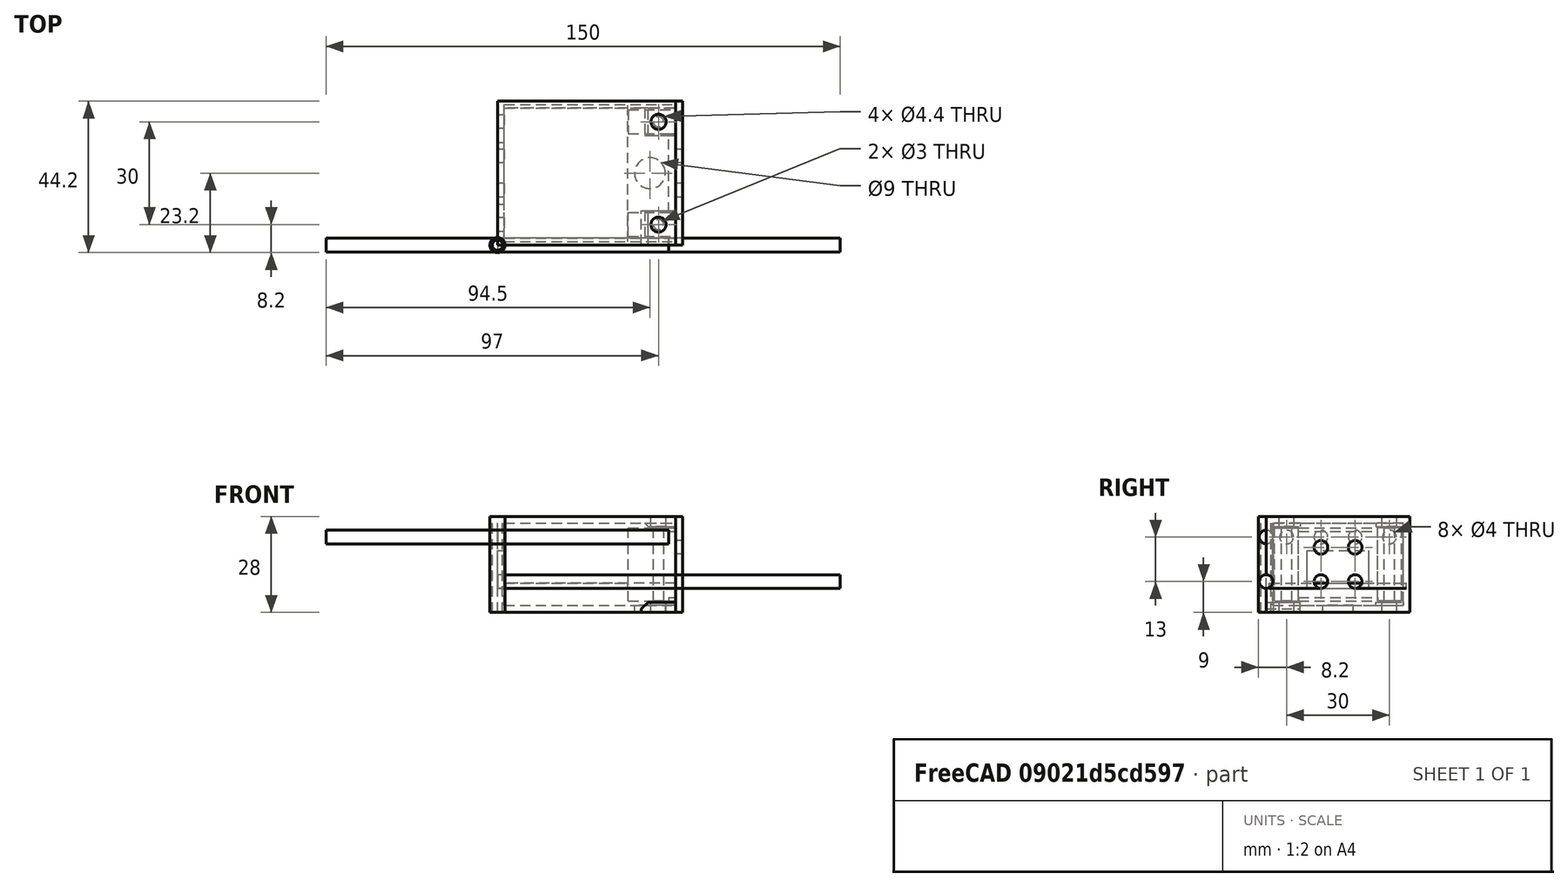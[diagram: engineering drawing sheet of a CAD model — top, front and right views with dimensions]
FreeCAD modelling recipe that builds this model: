
FCSTD DOCUMENT  (FreeCAD 0.19R)
Label: 220_5v_box
License: All rights reserved
LicenseURL: http://en.wikipedia.org/wiki/All_rights_reserved
objects: Part::Box×12, Part::Cylinder×5, Part::FeaturePython×5, Part::MultiFuse×4, Part::Mirroring×3, Part::Cut×3, Part::Chamfer×1
note: 28 computed .brp shape members not serialized (recipe doc carries the construction recipe); baked Part::Feature solids carry a one-line shape summary decoded from their .brp

FEATURE [Part::Box] Box  label="internal cube"
  AttacherType = Attacher::AttachEngine3D
  Height = 24
  Length = 50
  Placement = pos=(2,2,2) rot=(0,0,1;0rad)
  Width = 38
  expr: Width = <<pcb extract cube>>.Width - 2mm
  expr: Length = <<pcb extract cube>>.Length
FEATURE [Part::Box] Box001  label="pcb extract cube"
  AttacherType = Attacher::AttachEngine3D
  Height = 1.5
  Length = 50
  Placement = pos=(2,1,7) rot=(0,0,1;0rad)
  Width = 40
FEATURE [Part::Box] Box002  label="external cube"
  AttacherType = Attacher::AttachEngine3D
  Height = 28
  Length = 52
  Width = 42
  expr: Height = <<internal cube>>.Height + 4mm
  expr: Width = <<internal cube>>.Width + 4mm
  expr: Length = <<internal cube>>.Length + 2mm
FEATURE [Part::Box] Box003  label="pcb mockup"
  AttacherType = Attacher::AttachEngine3D
  Height = 1.5
  Length = 36
  Placement = pos=(2,1,7) rot=(0,0,1;0rad)
  Width = 40
FEATURE [Part::Box] Box004  label="usb hole cube"
  AttacherType = Attacher::AttachEngine3D
  Height = 11
  Length = 10
  Placement = pos=(0,12,7) rot=(0,0,1;0rad)
  Width = 18
  expr: .Placement.Base.y = <<pcb extract cube>>.Placement.Base.y + (<<pcb extract cube>>.Width - Width) / 2
  expr: .Placement.Base.z = <<pcb extract cube>>.Placement.Base.z
FEATURE [Part::Cylinder] Cylinder  label="wire hole"
  Angle = 360
  AttacherType = Attacher::AttachEngine3D
  Height = 10
  Placement = pos=(44.5,21,0) rot=(0,0,1;0rad)
  Radius = 4.5
  expr: .Placement.Base.x = <<pcb mockup>>.Length + 4mm + Radius
  expr: .Placement.Base.y = <<external cube>>.Width / 2
FEATURE [Part::Box] Box005  label="bolt hole stand"
  AttacherType = Attacher::AttachEngine3D
  Height = 3
  Length = 10
  Placement = pos=(42,0,0) rot=(0,0,1;0rad)
  Width = 10
  expr: .Placement.Base.x = <<external cube>>.Length - Length
FEATURE [Part::Chamfer] Chamfer  label="bolt hole stand chamfer"
  Base = -> Box005
  Edges = 1 edges r=2: [Edge2]
FEATURE [Part::FeaturePython] Array  label="bolt hole stand array"  # Draft array (typed FeaturePython)
  Angle = 360
  ArrayType = 0
  Axis = (0,0,1)
  Base = -> Chamfer
  Center = (0,0,0)
  Count = 2
  ExpandArray = false
  Fuse = false
  IntervalAxis = (0,0,0)
  IntervalX = (100,0,0)
  IntervalY = (0,32,0)
  IntervalZ = (0,0,100)
  NumberCircles = 3
  NumberPolar = 5
  NumberX = 1
  NumberY = 2
  NumberZ = 1
  PlacementList = 2 placements: [(0,0,0),(0,32,0)]
  RadialDistance = 50
  ScaleList = (2) [(1,1,1),(1,1,1)]
  Symmetry = 1
  TangentialDistance = 25
  expr: .IntervalY.y = <<external cube>>.Width - <<bolt hole stand>>.Width
FEATURE [Part::Mirroring] Part__Mirroring  label="bolt hole stand array (Mirror #1)"
  Base = (0,0,14)
  Normal = (0,0,1)
  Source = -> Array
  expr: .Base.z = <<external cube>>.Height / 2
FEATURE [Part::Cylinder] Cylinder001  label="insert hole"
  Angle = 360
  AttacherType = Attacher::AttachEngine3D
  Height = 28
  Radius = 2.2
  expr: Height = <<external cube>>.Height
FEATURE [Part::FeaturePython] Array001  label="bolt hole array"  # Draft array (typed FeaturePython)
  Angle = 360
  ArrayType = 0
  Axis = (0,0,1)
  Base = -> Cylinder001
  Center = (0,0,0)
  Count = 2
  ExpandArray = false
  Fuse = false
  IntervalAxis = (0,0,0)
  IntervalX = (100,0,0)
  IntervalY = (0,30,0)
  IntervalZ = (0,0,100)
  NumberCircles = 3
  NumberPolar = 5
  NumberX = 1
  NumberY = 2
  NumberZ = 1
  Placement = pos=(47,6,0) rot=(0,0,1;0rad)
  PlacementList = 2 placements: [(0,0,0),(0,30,0)]
  RadialDistance = 50
  ScaleList = (2) [(1,1,1),(1,1,1)]
  Symmetry = 1
  TangentialDistance = 25
  expr: .Placement.Base.y = (<<external cube>>.Width - .IntervalY.y) / 2
  expr: .Placement.Base.x = <<external cube>>.Length - 5mm
FEATURE [Part::Cylinder] Cylinder002  label="ventilation hole"
  Angle = 360
  AttacherType = Attacher::AttachEngine3D
  Height = 100
  Placement = pos=(50,0,22) rot=(-0.57735,-0.57735,0.57735;2.0944rad)
  Radius = 2
  expr: .Placement.Base.x = Height / 2
FEATURE [Part::FeaturePython] Array002  label="ventilation hole array"  # Draft array (typed FeaturePython)
  Angle = 360
  ArrayType = 0
  Axis = (0,0,1)
  Base = -> Cylinder002
  Center = (0,0,0)
  Count = 4
  ExpandArray = false
  Fuse = false
  IntervalAxis = (0,0,0)
  IntervalX = (100,0,0)
  IntervalY = (0,10,0)
  IntervalZ = (0,0,100)
  NumberCircles = 3
  NumberPolar = 5
  NumberX = 1
  NumberY = 4
  NumberZ = 1
  Placement = pos=(0,6,0) rot=(0,0,1;0rad)
  PlacementList = 4 placements: arithmetic series from (50,0,22) step (0,10,0) to (50,30,22)
  RadialDistance = 50
  ScaleList = (4) [(1,1,1),(1,1,1),(1,1,1),(1,1,1)]
  Symmetry = 1
  TangentialDistance = 25
  expr: .Placement.Base.y = (<<external cube>>.Width - .IntervalY.y * (NumberY - 1)) / 2
FEATURE [Part::MultiFuse] Fusion  label="extract fusion"
  Shapes = -> [Box001,Box,Box004,Cylinder,Array002]
FEATURE [Part::Cut] Cut  label="body cut"
  Base = -> Box002
  Tool = -> Fusion
FEATURE [Part::MultiFuse] Fusion001  label="full body fusion"
  Shapes = -> [Cut,Part__Mirroring,Array]
FEATURE [Part::Cut] Cut001  label="full body cut"
  Base = -> Fusion001
  Tool = -> Array001
FEATURE [Part::Box] Box006  label="wall cube"
  AttacherType = Attacher::AttachEngine3D
  Height = 28
  Length = 2
  Placement = pos=(52,0,0) rot=(0,0,1;0rad)
  Width = 42
  expr: .Placement.Base.x = <<external cube>>.Length
  expr: Height = <<external cube>>.Height
  expr: Width = <<external cube>>.Width
FEATURE [Part::Box] Box007  label="wall side"
  AttacherType = Attacher::AttachEngine3D
  Height = 21.4
  Length = 13.8
  Placement = pos=(38.2,2.5,3.3) rot=(0,0,1;0rad)
  Width = 7
  expr: .Placement.Base.z = (<<external cube>>.Height - Height) / 2
  expr: .Placement.Base.x = <<external cube>>.Length - Length
FEATURE [Part::Cylinder] Cylinder003  label="bolt hole"
  Angle = 360
  AttacherType = Attacher::AttachEngine3D
  Height = 28
  Radius = 1.5
  expr: Height = <<external cube>>.Height
FEATURE [Part::FeaturePython] Array003  label="bolt hole array001"  # Draft array (typed FeaturePython)
  Angle = 360
  ArrayType = 0
  Axis = (0,0,1)
  Base = -> Cylinder003
  Center = (0,0,0)
  Count = 2
  ExpandArray = false
  Fuse = false
  IntervalAxis = (0,0,0)
  IntervalX = (100,0,0)
  IntervalY = (0,30,0)
  IntervalZ = (0,0,100)
  NumberCircles = 3
  NumberPolar = 5
  NumberX = 1
  NumberY = 2
  NumberZ = 1
  Placement = pos=(47,6,0) rot=(0,0,1;0rad)
  PlacementList = 2 placements: [(0,0,0),(0,30,0)]
  RadialDistance = 50
  ScaleList = (2) [(1,1,1),(1,1,1)]
  Symmetry = 1
  TangentialDistance = 25
  expr: .Placement.Base.x = <<external cube>>.Length - 5mm
  expr: .Placement.Base.y = (<<external cube>>.Width - .IntervalY.y) / 2
FEATURE [Part::Mirroring] Part__Mirroring001  label="wall side (Mirror #2)"
  Base = (0,21,0)
  Normal = (0,1,0)
  Source = -> Box007
  expr: .Base.y = <<external cube>>.Width / 2
FEATURE [Part::Box] Box008  label="y_wall"
  AttacherType = Attacher::AttachEngine3D
  Height = 1
  Length = 2
  Placement = pos=(50,3,3.3) rot=(0,0,1;0rad)
  Width = 36
  expr: .Placement.Base.z = <<wall side>>.Placement.Base.z
  expr: .Placement.Base.x = <<external cube>>.Length - Length
  expr: .Placement.Base.y = (<<external cube>>.Width - Width) / 2
  expr: Width = <<internal cube>>.Width - 2mm
FEATURE [Part::Mirroring] Part__Mirroring002  label="y_wall (Mirror #3)"
  Base = (0,0,14)
  Normal = (0,0,1)
  Source = -> Box008
  expr: .Base.z = <<external cube>>.Height / 2
FEATURE [Part::MultiFuse] Fusion002  label="wall fusion"
  Shapes = -> [Box007,Part__Mirroring001,Box006,Part__Mirroring002,Box008]
FEATURE [Part::Box] Box009  label="internal cube001"
  AttacherType = Attacher::AttachEngine3D
  Height = 24
  Length = 50
  Placement = pos=(2,2,2) rot=(0,0,1;0rad)
  Width = 38
  expr: Length = <<pcb extract cube001>>.Length
  expr: Width = <<pcb extract cube001>>.Width - 2mm
FEATURE [Part::Box] Box010  label="pcb extract cube001"
  AttacherType = Attacher::AttachEngine3D
  Height = 1.5
  Length = 50
  Placement = pos=(2,1,7) rot=(0,0,1;0rad)
  Width = 40
FEATURE [Part::Box] Box011  label="external cube001"
  AttacherType = Attacher::AttachEngine3D
  Height = 28
  Length = 52
  Width = 42
  expr: Length = <<internal cube001>>.Length + 2mm
  expr: Width = <<internal cube001>>.Width + 4mm
  expr: Height = <<internal cube001>>.Height + 4mm
FEATURE [Part::Cylinder] Cylinder004  label="ventilation hole001"
  Angle = 360
  AttacherType = Attacher::AttachEngine3D
  Height = 100
  Placement = pos=(100,0,9) rot=(0.57735,0.57735,-0.57735;4.18879rad)
  Radius = 2
  expr: .Placement.Base.x = Height
FEATURE [Part::FeaturePython] Array004  label="ventilation hole array001"  # Draft array (typed FeaturePython)
  Angle = 360
  ArrayType = 0
  Axis = (0,0,1)
  Base = -> Cylinder004
  Center = (0,0,0)
  Count = 4
  ExpandArray = false
  Fuse = false
  IntervalAxis = (0,0,0)
  IntervalX = (100,0,0)
  IntervalY = (0,10,0)
  IntervalZ = (0,0,10)
  NumberCircles = 3
  NumberPolar = 5
  NumberX = 1
  NumberY = 2
  NumberZ = 2
  Placement = pos=(0,16,0) rot=(0,0,1;0rad)
  PlacementList = 4 placements: [(100,0,9),(100,0,19),(100,10,9),(100,10,19)]
  RadialDistance = 50
  ScaleList = (4) [(1,1,1),(1,1,1),(1,1,1),(1,1,1)]
  Symmetry = 1
  TangentialDistance = 25
  expr: .Placement.Base.y = (<<external cube001>>.Width - .IntervalY.y * (NumberY - 1)) / 2
FEATURE [Part::MultiFuse] Fusion003  label="wall hole fusion"
  Shapes = -> [Array004,Array003]
FEATURE [Part::Cut] Cut002  label="wall cut"
  Base = -> Fusion002
  Tool = -> Fusion003
